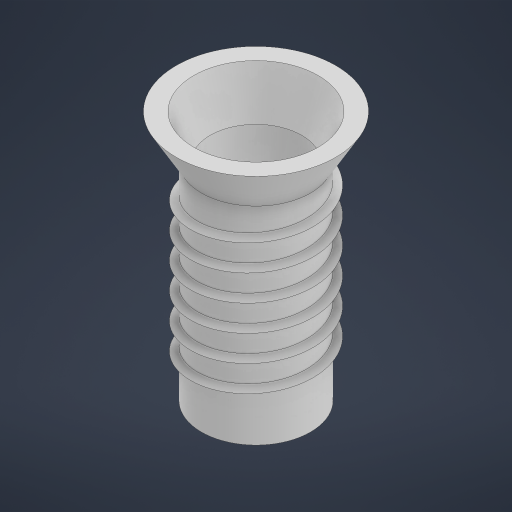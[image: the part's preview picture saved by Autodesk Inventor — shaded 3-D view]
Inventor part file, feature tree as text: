
AUTODESK INVENTOR PART (.ipt)
format: ipt  version: 2024.1 (Build 281209000, 209)  size: 323,072 bytes
history: native  units: mm
features: sketch x3, revolve x2, helix x1
ambient origin geometry x8: Origin, YZ Plane, XZ Plane, XY Plane, X Axis, Y Axis, Z Axis, Center Point
bodies: Solid1 (feature_tree)
feature tree (6):
  revolve  "Revolution1"  [1 undecoded]
  helix  "Coil1"  [1 undecoded]
  revolve  "Revolution2"  [1 undecoded]
  sketch  "Sketch1"  dims[d0=2.5mm d1=12.5mm d2=8.0mm]
  sketch  "Sketch2"  dims[d3=2.0mm d4=47.5mm]
  sketch  "Sketch3"  dims[d5=90.0deg d6=60.0deg d7=1.8mm d8=3.0mm d9=6.0mm d10=10.0mm d11=60.0mm d12=0.0mm d13=90.0deg d14=90.0deg d15=0.0mm d16=0.0mm d17=120.0deg d18=4.0mm d19=10.0mm d20=90.0deg]
note: 3 required parameter values undecoded (feature->parameter linkage not recoverable at this tier; creation-order binding heuristic only, values carry confidence <= 0.55)